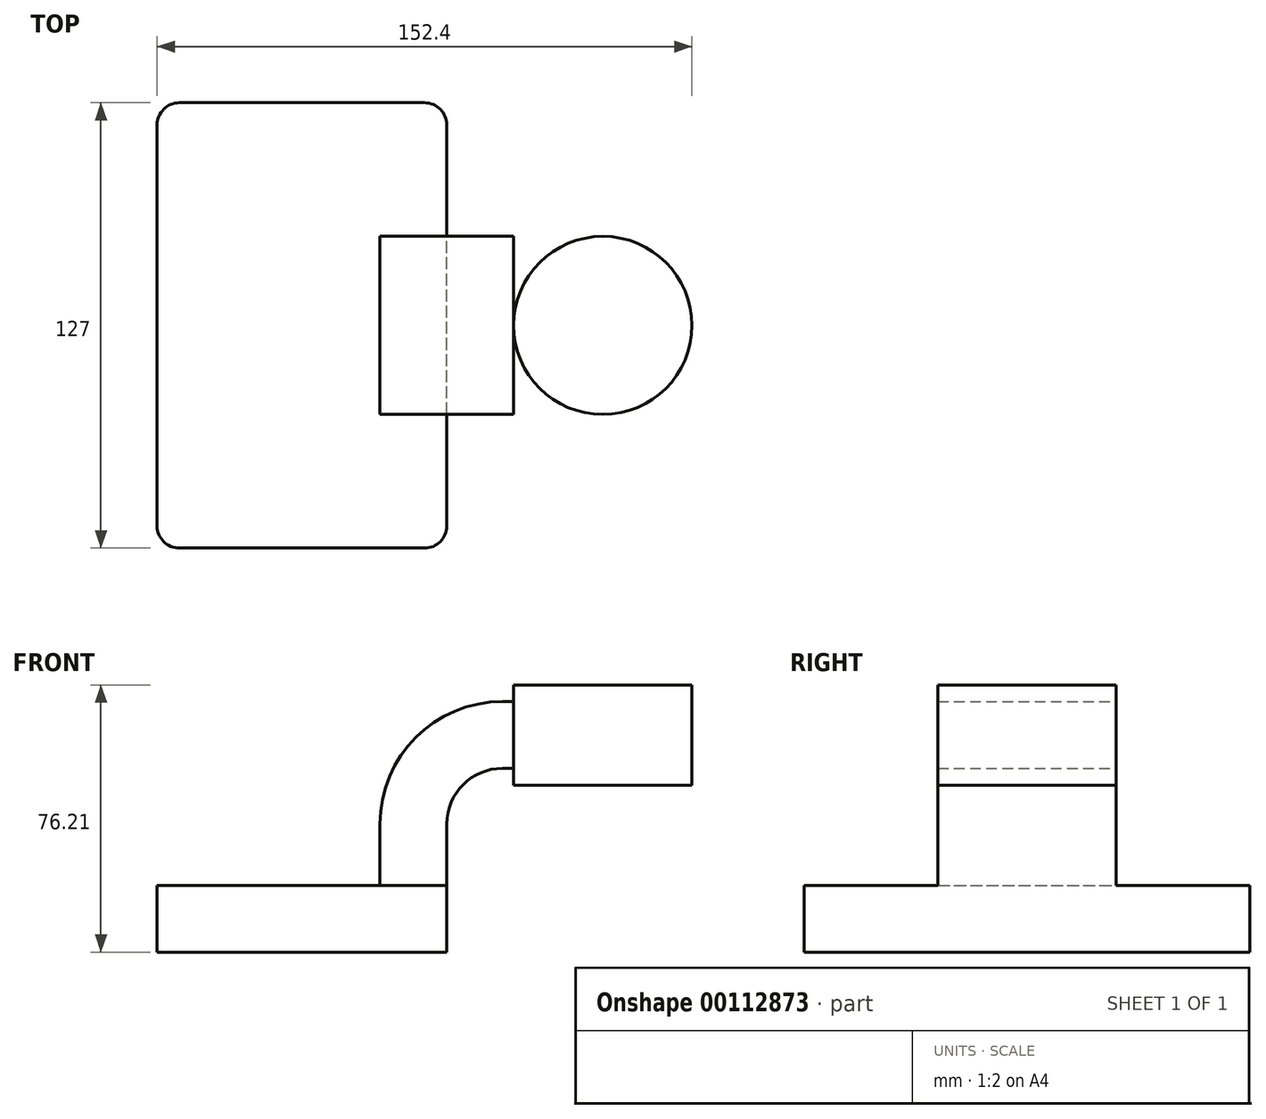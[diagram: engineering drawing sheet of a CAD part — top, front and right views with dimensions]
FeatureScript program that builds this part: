
annotation { "Feature Type Name" : "Feature", "Feature Type Description" : "" }
export const myFeature = defineFeature(function(context is Context, id is Id, definition is map)
    precondition{}
    {
        {
            var Q0;
            Q0=qCreatedBy(makeId("Front.planeOp"),FACE);
            var sketch = newSketch(context, id + "F0", { "sketchPlane" : qUnion([Q0])});
            skLineSegment(sketch, "E0.bottom", {"start": v(-41.28, 9.52) * mm, "end": v(41.28, 9.53) * mm});
            skLineSegment(sketch, "E0.top", {"start": v(-41.28, -9.53) * mm, "end": v(41.28, -9.52) * mm});
            skLineSegment(sketch, "E0.left", {"start": v(-41.28, 9.52) * mm, "end": v(-41.28, -9.53) * mm});
            skLineSegment(sketch, "E0.right", {"start": v(41.28, 9.53) * mm, "end": v(41.28, -9.52) * mm});
            skPoint(sketch, "E0.middle", {"position": v(0, 0) * mm});
            skLineSegment(sketch, "E1.bottom", {"start": v(60.33, 38.1) * mm, "end": v(111.13, 38.1) * mm});
            skLineSegment(sketch, "E1.top", {"start": v(60.33, 66.67) * mm, "end": v(111.12, 66.67) * mm});
            skLineSegment(sketch, "E1.left", {"start": v(60.33, 38.1) * mm, "end": v(60.33, 66.68) * mm});
            skLineSegment(sketch, "E1.right", {"start": v(111.13, 38.1) * mm, "end": v(111.13, 66.68) * mm});
            skPoint(sketch, "E1.middle", {"position": v(85.73, 52.39) * mm});
            skLineSegment(sketch, "E2", {"start": v(41.28, 9.53) * mm, "end": v(41.28, 27) * mm});
            skArc(sketch, "E3", {"start": v(41.28, 27) * mm, "mid": v(45.92, 38.23) * mm, "end": v(57.15, 42.88) * mm});
            skLineSegment(sketch, "E4", {"start": v(85.73, 52.39) * mm, "end": v(85.73, -9.8) * mm});
            skPoint(sketch, "E4.endSnap0", {"position": v(85.73, 38.1) * mm});
            skLineSegment(sketch, "E5", {"start": v(57.15, 42.88) * mm, "end": v(85.73, 42.88) * mm});
            skLineSegment(sketch, "E6.0", {"start": v(57.15, 61.93) * mm, "end": v(85.73, 61.93) * mm});
            skArc(sketch, "E6.1", {"start": v(22.23, 27) * mm, "mid": v(32.45, 51.7) * mm, "end": v(57.15, 61.93) * mm});
            skLineSegment(sketch, "E6.2", {"start": v(22.23, 9.53) * mm, "end": v(22.23, 27) * mm});
            skLineSegment(sketch, "E7", {"start": v(85.73, 66.67) * mm, "end": v(85.73, 38.1) * mm});
            skFitSpline(sketch, "E8", {"points": [v(-41.28, 9.53) * mm, v(57.15, 61.93) * mm], "startDerivative": vector(-0.9, 117.16) * mm, "endDerivative": vector(102.6, -3.32) * mm});
            skSolve(sketch);
        }
        {
            var Q0;
            Q0=makeQuery(id+"F0.imprint","IMPRINT",FACE,{"disambiguationData":[TD([[makeQuery(id+"F0.imprint","IMPRINT",EDGE,{"derivedFrom":sQuery(id+"F0.wireOp",EDGE,"E0.top")}),1.0]])]});
            extrude(context, id + "F1", {"entities" : qUnion([Q0]), "endBound" : BoundingType.SYMMETRIC, "depth" : 127 * mm});
        }
        {
            var Q0;
            {var subQ2=sQuery(id+"F0.wireOp",EDGE,"E2");Q0=makeQuery(id+"F0.imprint","IMPRINT",FACE,{"disambiguationData":[TD([[makeQuery(id+"F0.imprint","IMPRINT",EDGE,{"derivedFrom":subQ2}),1.0]])]});}
            var Q1;
            {var subQ0=sQuery(id+"F0.wireOp",EDGE,"E7");var subQ3=makeQuery(id+"F0.imprint","IMPRINT",VERTEX,{"derivedFrom":subQ0});Q1=makeQuery(id+"F0.imprint","IMPRINT",FACE,{"disambiguationData":[TD([[makeQuery(id+"F0.imprint","IMPRINT",EDGE,{"disambiguationData":[TD([[subQ3,1.0]])],"derivedFrom":subQ0}),-1.0]])]});}
            extrude(context, id + "F2", {"entities" : qUnion([Q0, Q1]), "operationType" : NewBodyOperationType.ADD, "endBound" : BoundingType.SYMMETRIC, "depth" : 50.8 * mm});
        }
        {
            var Q0;
            Q0=makeQuery(id+"F0.imprint","IMPRINT",FACE,{"disambiguationData":[TD([[makeQuery(id+"F0.imprint","IMPRINT",EDGE,{"derivedFrom":sQuery(id+"F0.wireOp",EDGE,"E6.1")}),1.0]])]});
            extrude(context, id + "F3", {"entities" : qUnion([Q0]), "operationType" : NewBodyOperationType.ADD, "endBound" : BoundingType.SYMMETRIC, "depth" : 15.88 * mm});
        }
        {
            var Q0;
            {var subQ0=sQuery(id+"F0.wireOp",EDGE,"E1.right");Q0=makeQuery(id+"F0.imprint","IMPRINT",FACE,{"disambiguationData":[TD([[makeQuery(id+"F0.imprint","IMPRINT",EDGE,{"derivedFrom":subQ0}),1.0]])]});}
            var Q1;
            Q1=sQuery(id+"F0.wireOp",EDGE,"E4");
            revolve(context, id + "F4", {"operationType" : NewBodyOperationType.ADD, "entities" : qUnion([Q0]), "axis" : qUnion([Q1]), "revolveType" : RevolveType.FULL});
        }
        {
            var Q0;
            Q0=makeQuery(id+"F1.opExtrude","CAP_EDGE",EDGE,{"disambiguationData":[OSD([sQuery(id+"F0.wireOp",EDGE,"E0.right")])],"isStart":false});
            var Q1;
            Q1=makeQuery(id+"F1.opExtrude","CAP_EDGE",EDGE,{"disambiguationData":[OSD([sQuery(id+"F0.wireOp",EDGE,"E0.left")])],"isStart":false});
            var Q2;
            Q2=makeQuery(id+"F1.opExtrude","CAP_EDGE",EDGE,{"disambiguationData":[OSD([sQuery(id+"F0.wireOp",EDGE,"E0.left")])],"isStart":true});
            var Q3;
            Q3=makeQuery(id+"F1.opExtrude","CAP_EDGE",EDGE,{"disambiguationData":[OSD([sQuery(id+"F0.wireOp",EDGE,"E0.right")])],"isStart":true});
            fillet(context, id + "F5", {"entities" : qUnion([Q0, Q1, Q2, Q3]), "radius" : 6.35 * mm, "tangentPropagation" : true, "allowEdgeOverflow" : false});
        }
    });
